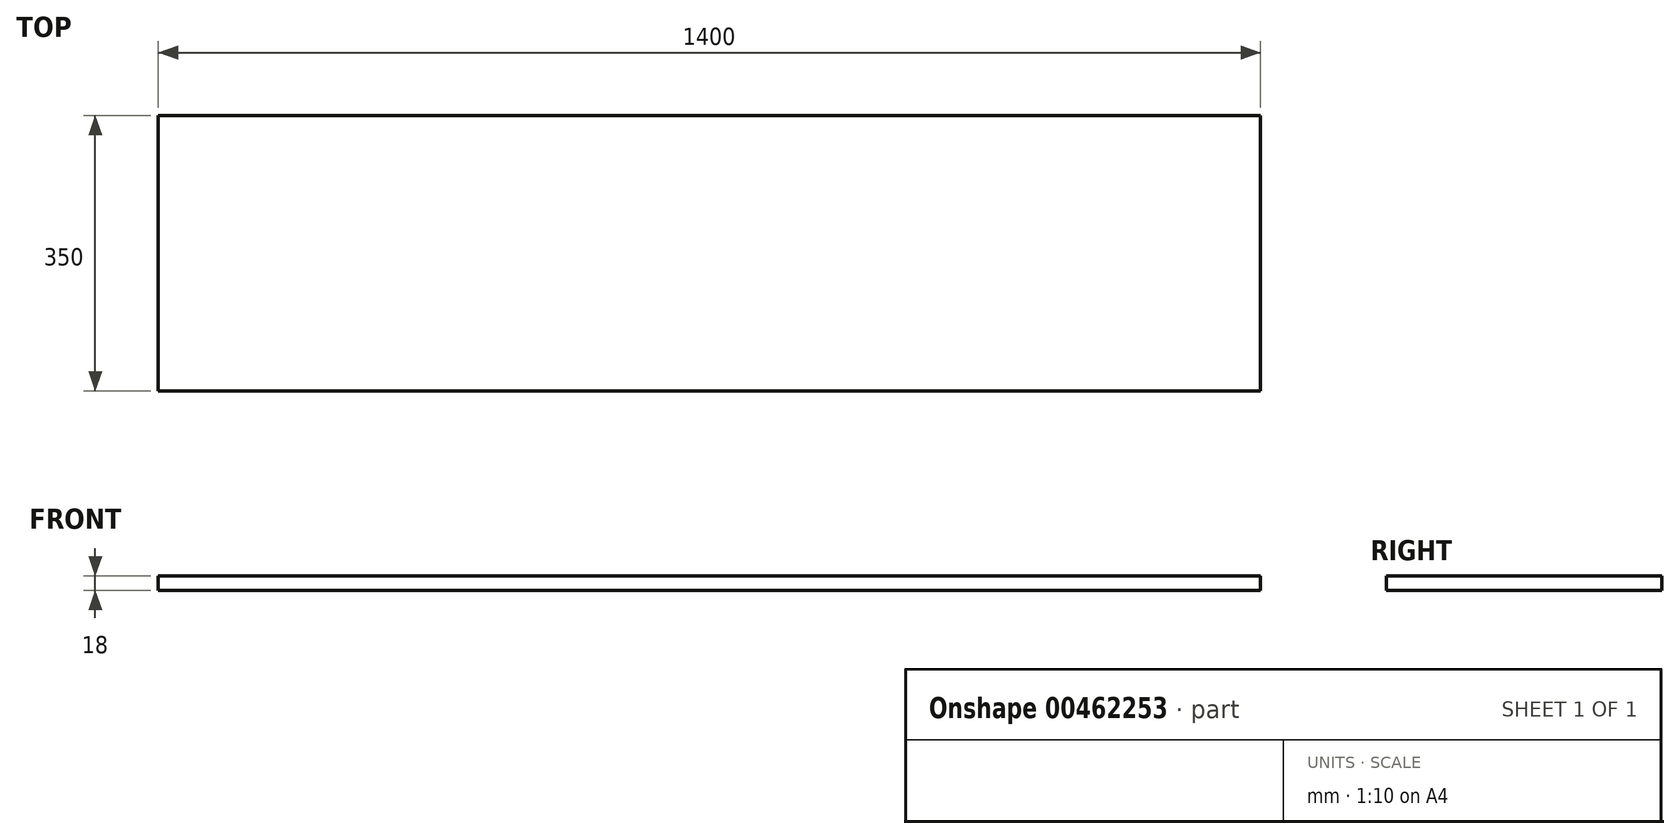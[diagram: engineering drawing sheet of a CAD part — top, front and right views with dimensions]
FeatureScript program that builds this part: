
annotation { "Feature Type Name" : "Feature", "Feature Type Description" : "" }
export const myFeature = defineFeature(function(context is Context, id is Id, definition is map)
    precondition{}
    {
        {
            var Q0;
            Q0=qCreatedBy(makeId("Top.planeOp"),FACE);
            var sketch = newSketch(context, id + "F0", { "sketchPlane" : qUnion([Q0])});
            skLineSegment(sketch, "E0.bottom", {"start": v(700, -175) * mm, "end": v(-700, -175) * mm});
            skLineSegment(sketch, "E0.top", {"start": v(700, 175) * mm, "end": v(-700, 175) * mm});
            skLineSegment(sketch, "E0.left", {"start": v(700, -175) * mm, "end": v(700, 175) * mm});
            skLineSegment(sketch, "E0.right", {"start": v(-700, -175) * mm, "end": v(-700, 175) * mm});
            skPoint(sketch, "E0.middle", {"position": v(0, 0) * mm});
            skSolve(sketch);
        }
        {
            var Q0;
            Q0=makeQuery(id+"F0.imprint","IMPRINT",FACE,{"disambiguationData":[TD([[makeQuery(id+"F0.imprint","IMPRINT",EDGE,{"derivedFrom":sQuery(id+"F0.wireOp",EDGE,"E0.bottom")}),-1.0]])]});
            extrude(context, id + "F1", {"entities" : qUnion([Q0]), "depth" : 18 * mm});
        }
    });
